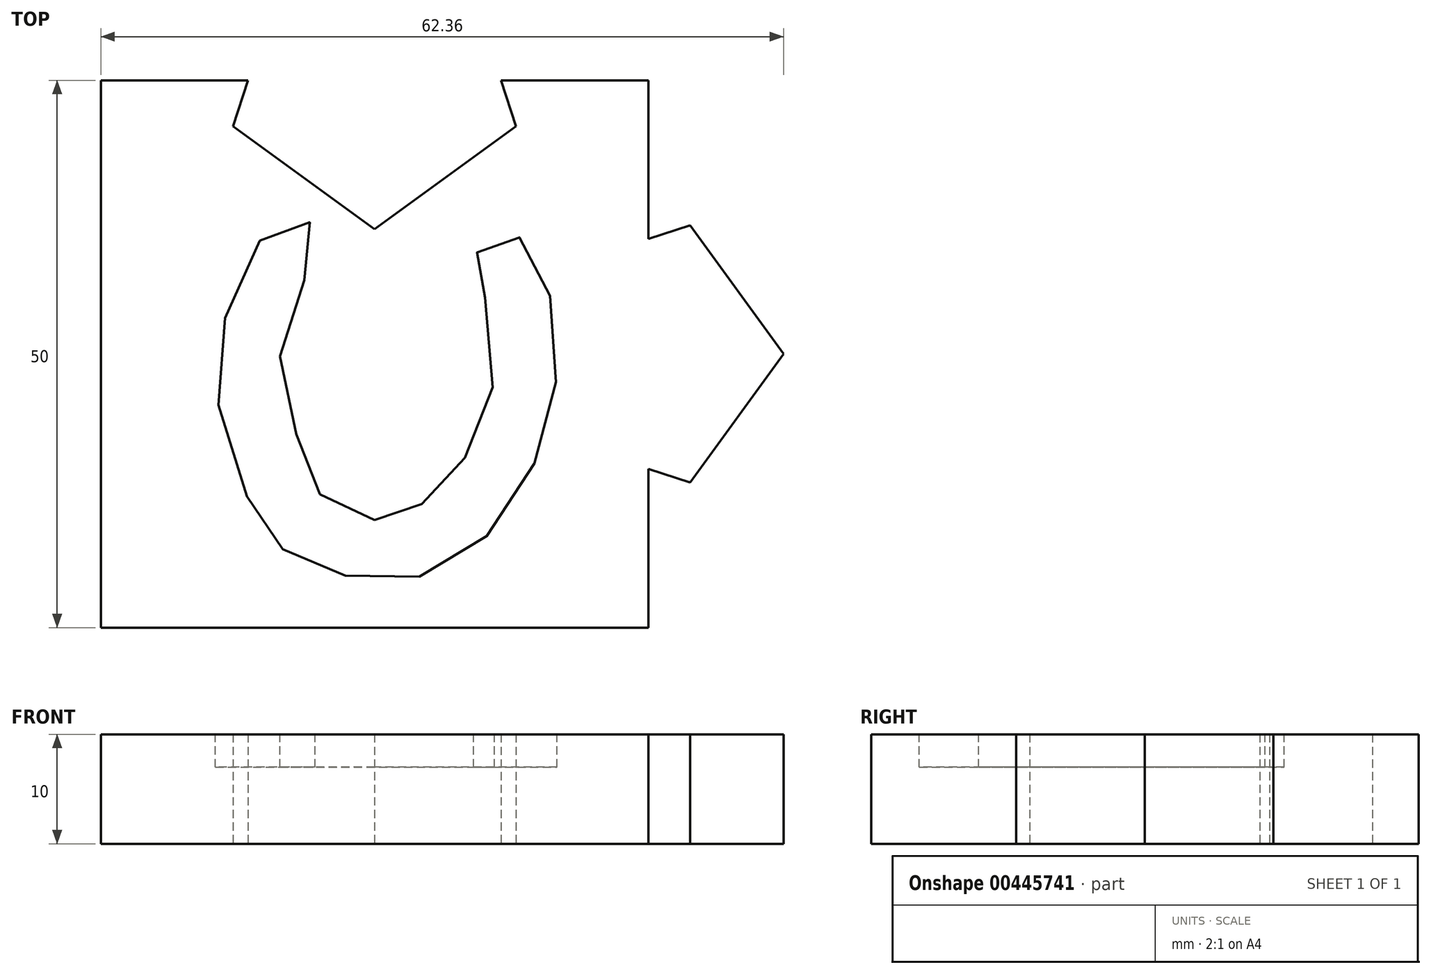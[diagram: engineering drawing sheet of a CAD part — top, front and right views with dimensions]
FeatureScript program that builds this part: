
annotation { "Feature Type Name" : "Feature", "Feature Type Description" : "" }
export const myFeature = defineFeature(function(context is Context, id is Id, definition is map)
    precondition{}
    {
        {
            var Q0;
            Q0=qCreatedBy(makeId("Top.planeOp"),FACE);
            var sketch = newSketch(context, id + "F0", { "sketchPlane" : qUnion([Q0])});
            skLineSegment(sketch, "E0.bottom", {"start": v(25, -25) * mm, "end": v(-25, -25) * mm});
            skLineSegment(sketch, "E0.top", {"start": v(25, 25) * mm, "end": v(-25, 25) * mm});
            skLineSegment(sketch, "E0.left", {"start": v(25, -25) * mm, "end": v(25, 25) * mm});
            skLineSegment(sketch, "E0.right", {"start": v(-25, -25) * mm, "end": v(-25, 25) * mm});
            skPoint(sketch, "E0.middle", {"position": v(0, 0) * mm});
            skLineSegment(sketch, "E1", {"start": v(25, 25) * mm, "end": v(15, 25) * mm, "construction": true});
            skLineSegment(sketch, "E2", {"start": v(15, 25) * mm, "end": v(15, -25) * mm, "construction": true});
            skCircle(sketch, "E3.cCircle", {"center": v(25, 0) * mm, "radius": 10 * mm, "construction": true});
            skLineSegment(sketch, "E3.0", {"start": v(15, -7.27) * mm, "end": v(15, 7.27) * mm});
            skLineSegment(sketch, "E3.1", {"start": v(15, 7.27) * mm, "end": v(28.82, 11.76) * mm});
            skLineSegment(sketch, "E3.2", {"start": v(28.82, 11.76) * mm, "end": v(37.36, 0) * mm});
            skLineSegment(sketch, "E3.3", {"start": v(37.36, 0) * mm, "end": v(28.82, -11.76) * mm});
            skLineSegment(sketch, "E3.4", {"start": v(28.82, -11.76) * mm, "end": v(15, -7.27) * mm});
            skPoint(sketch, "E3.0.midPoint", {"position": v(15, 0) * mm});
            skLineSegment(sketch, "E4", {"start": v(-25, 25) * mm, "end": v(-25, 36) * mm, "construction": true});
            skLineSegment(sketch, "E5", {"start": v(-25, 36) * mm, "end": v(25, 36) * mm, "construction": true});
            skCircle(sketch, "E6.cCircle", {"center": v(0, 25) * mm, "radius": 11 * mm, "construction": true});
            skLineSegment(sketch, "E6.0", {"start": v(-8, 36) * mm, "end": v(8, 36) * mm});
            skLineSegment(sketch, "E6.1", {"start": v(8, 36) * mm, "end": v(12.93, 20.8) * mm});
            skLineSegment(sketch, "E6.2", {"start": v(12.93, 20.8) * mm, "end": v(0, 11.4) * mm});
            skLineSegment(sketch, "E6.3", {"start": v(0, 11.4) * mm, "end": v(-12.93, 20.8) * mm});
            skLineSegment(sketch, "E6.4", {"start": v(-12.93, 20.8) * mm, "end": v(-8, 36) * mm});
            skPoint(sketch, "E6.0.midPoint", {"position": v(0, 36) * mm});
            skSolve(sketch);
        }
        {
            var Q0;
            {var subQ10=sQuery(id+"F0.wireOp",EDGE,"E0.bottom");Q0=makeQuery(id+"F0.imprint","IMPRINT",FACE,{"disambiguationData":[TD([[makeQuery(id+"F0.imprint","IMPRINT",EDGE,{"derivedFrom":subQ10}),-1.0]])]});}
            var Q1;
            {var subQ1=sQuery(id+"F0.wireOp",EDGE,"E3.2");Q1=makeQuery(id+"F0.imprint","IMPRINT",FACE,{"disambiguationData":[TD([[makeQuery(id+"F0.imprint","IMPRINT",EDGE,{"derivedFrom":subQ1}),-1.0]])]});}
            var Q2;
            {var subQ5=sQuery(id+"F0.wireOp",EDGE,"E3.0");Q2=makeQuery(id+"F0.imprint","IMPRINT",FACE,{"disambiguationData":[TD([[makeQuery(id+"F0.imprint","IMPRINT",EDGE,{"derivedFrom":subQ5}),-1.0]])]});}
            extrude(context, id + "F1", {"entities" : qUnion([Q0, Q1, Q2]), "depth" : 10 * mm});
        }
        {
            var Q0;
            Q0=makeQuery(id+"F1.opExtrude","CAP_FACE",FACE,{"disambiguationData":[OSD([sQuery(id+"F0.wireOp",EDGE,"E0.bottom"),sQuery(id+"F0.wireOp",EDGE,"E0.top"),sQuery(id+"F0.wireOp",EDGE,"E0.left"),sQuery(id+"F0.wireOp",EDGE,"E0.right"),sQuery(id+"F0.wireOp",EDGE,"E3.1"),sQuery(id+"F0.wireOp",EDGE,"E3.2"),sQuery(id+"F0.wireOp",EDGE,"E3.3"),sQuery(id+"F0.wireOp",EDGE,"E3.4"),sQuery(id+"F0.wireOp",EDGE,"E6.1"),sQuery(id+"F0.wireOp",EDGE,"E6.2"),sQuery(id+"F0.wireOp",EDGE,"E6.3"),sQuery(id+"F0.wireOp",EDGE,"E6.4")])],"isStart":false});
            var sketch = newSketch(context, id + "F2", { "sketchPlane" : qUnion([Q0])});
            skFitSpline(sketch, "E7", {"points": [v(0, -15.16) * mm, v(-2.72, -14.04) * mm, v(-5.17, -12.65) * mm, v(-6.32, -10.47) * mm, v(-7.6, -5.6) * mm, v(-8.63, -0.78) * mm, v(-7.6, 4.28) * mm, v(-5.71, 8.38) * mm, v(-5.55, 10.96) * mm, v(-6.64, 12.69) * mm, v(-9.52, 11.44) * mm, v(-11.74, 8.05) * mm, v(-14.14, 1.56) * mm, v(-14.32, -4.3) * mm, v(-12.22, -11.67) * mm, v(-10.26, -15.75) * mm, v(-8.46, -17.79) * mm, v(-5.3, -19.6) * mm, v(-1.41, -20.43) * mm, v(3.01, -20.53) * mm, v(7.48, -19.04) * mm, v(11.54, -15.05) * mm, v(14.64, -9.88) * mm, v(16.3, -4.72) * mm, v(16.58, 1.8) * mm, v(15.6, 6.85) * mm, v(14.02, 10.1) * mm, v(11.86, 10.97) * mm, v(10.1, 10.32) * mm, v(9.13, 8.55) * mm, v(9.27, 6.58) * mm, v(10.02, 5.3) * mm, v(10.94, -0.93) * mm, v(9.9, -6.4) * mm, v(7.77, -10.14) * mm, v(5.19, -13.01) * mm, v(3.97, -13.92) * mm, v(2.36, -14.62) * mm, v(0, -15.16) * mm]});
            skSolve(sketch);
        }
        {
            var Q0;
            Q0=makeQuery(id+"F2.imprint","IMPRINT",FACE,{"disambiguationData":[TD([[makeQuery(id+"F2.imprint","IMPRINT",EDGE,{"derivedFrom":sQuery(id+"F2.wireOp",EDGE,"E7")}),1.0]])]});
            extrude(context, id + "F3", {"entities" : qUnion([Q0]), "operationType" : NewBodyOperationType.REMOVE, "oppositeDirection" : true, "depth" : 3 * mm});
        }
    });
